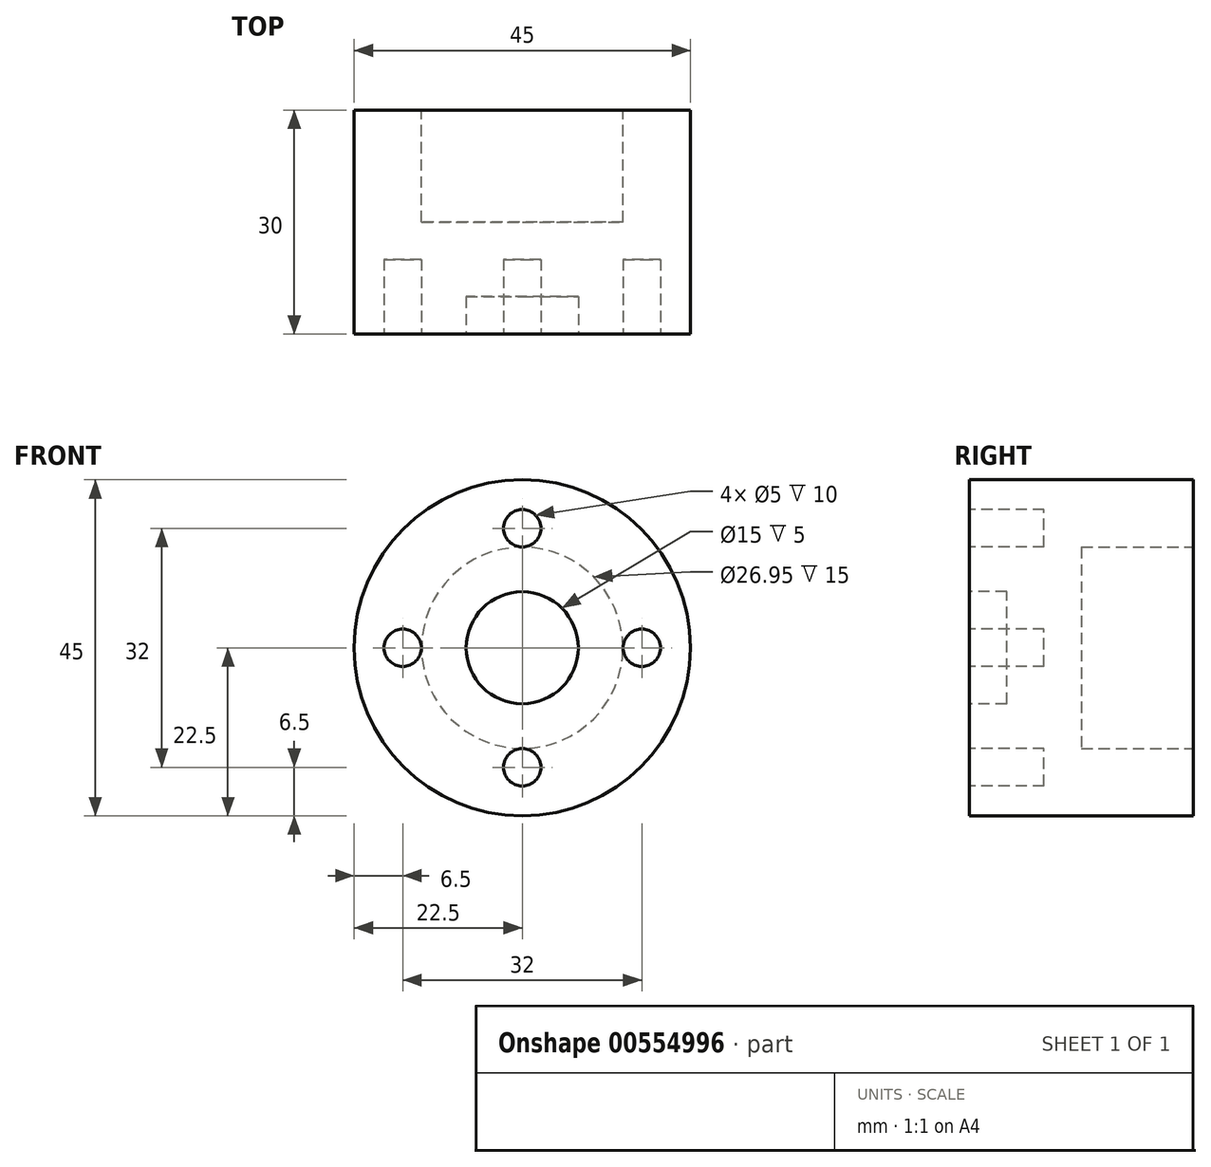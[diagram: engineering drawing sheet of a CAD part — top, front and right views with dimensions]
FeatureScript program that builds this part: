
annotation { "Feature Type Name" : "Feature", "Feature Type Description" : "" }
export const myFeature = defineFeature(function(context is Context, id is Id, definition is map)
    precondition{}
    {
        {
            var Q0;
            Q0=qCreatedBy(makeId("Front.planeOp"),FACE);
            var sketch = newSketch(context, id + "F0", { "sketchPlane" : qUnion([Q0])});
            skCircle(sketch, "E0", {"center": v(0, 0) * mm, "radius": 22.5 * mm});
            skSolve(sketch);
        }
        {
            var Q0;
            Q0=makeQuery(id+"F0.imprint","IMPRINT",FACE,{"disambiguationData":[TD([[makeQuery(id+"F0.imprint","IMPRINT",EDGE,{"derivedFrom":sQuery(id+"F0.wireOp",EDGE,"E0")}),1.0]])]});
            extrude(context, id + "F1", {"entities" : qUnion([Q0]), "depth" : 30 * mm, "offsetDistance" : 25 * mm});
        }
        {
            var Q0;
            Q0=makeQuery(id+"F1.opExtrude","CAP_FACE",FACE,{"disambiguationData":[OSD([sQuery(id+"F0.wireOp",EDGE,"E0")])],"isStart":false});
            var sketch = newSketch(context, id + "F2", { "sketchPlane" : qUnion([Q0])});
            skCircle(sketch, "E1", {"center": v(0, 0) * mm, "radius": 7.5 * mm});
            skSolve(sketch);
        }
        {
            var Q0;
            Q0=makeQuery(id+"F2.imprint","IMPRINT",FACE,{"disambiguationData":[TD([[makeQuery(id+"F2.imprint","IMPRINT",EDGE,{"derivedFrom":sQuery(id+"F2.wireOp",EDGE,"E1")}),1.0]])]});
            extrude(context, id + "F3", {"entities" : qUnion([Q0]), "operationType" : NewBodyOperationType.REMOVE, "oppositeDirection" : true, "depth" : 5 * mm, "offsetDistance" : 25 * mm});
        }
        {
            var Q0;
            Q0=makeQuery(id+"F1.opExtrude","CAP_FACE",FACE,{"disambiguationData":[OSD([sQuery(id+"F0.wireOp",EDGE,"E0")])],"isStart":false});
            var sketch = newSketch(context, id + "F4", { "sketchPlane" : qUnion([Q0])});
            skCircle(sketch, "E2", {"center": v(0, 16) * mm, "radius": 2.5 * mm});
            skCircle(sketch, "E3", {"center": v(0, -16) * mm, "radius": 2.5 * mm});
            skCircle(sketch, "E4", {"center": v(16, 0) * mm, "radius": 2.5 * mm});
            skCircle(sketch, "E5", {"center": v(-16, 0) * mm, "radius": 2.5 * mm});
            skSolve(sketch);
        }
        {
            var Q0;
            Q0=makeQuery(id+"F4.imprint","IMPRINT",FACE,{"disambiguationData":[TD([[makeQuery(id+"F4.imprint","IMPRINT",EDGE,{"derivedFrom":sQuery(id+"F4.wireOp",EDGE,"E5")}),1.0]])]});
            var Q1;
            Q1=makeQuery(id+"F4.imprint","IMPRINT",FACE,{"disambiguationData":[TD([[makeQuery(id+"F4.imprint","IMPRINT",EDGE,{"derivedFrom":sQuery(id+"F4.wireOp",EDGE,"E2")}),1.0]])]});
            var Q2;
            Q2=makeQuery(id+"F4.imprint","IMPRINT",FACE,{"disambiguationData":[TD([[makeQuery(id+"F4.imprint","IMPRINT",EDGE,{"derivedFrom":sQuery(id+"F4.wireOp",EDGE,"E4")}),1.0]])]});
            var Q3;
            Q3=makeQuery(id+"F4.imprint","IMPRINT",FACE,{"disambiguationData":[TD([[makeQuery(id+"F4.imprint","IMPRINT",EDGE,{"derivedFrom":sQuery(id+"F4.wireOp",EDGE,"E3")}),1.0]])]});
            extrude(context, id + "F5", {"entities" : qUnion([Q0, Q1, Q2, Q3]), "operationType" : NewBodyOperationType.REMOVE, "oppositeDirection" : true, "depth" : 10 * mm, "offsetDistance" : 25 * mm});
        }
        {
            var Q0;
            Q0=makeQuery(id+"F1.opExtrude","CAP_FACE",FACE,{"disambiguationData":[OSD([sQuery(id+"F0.wireOp",EDGE,"E0")])],"isStart":true});
            var sketch = newSketch(context, id + "F6", { "sketchPlane" : qUnion([Q0])});
            skCircle(sketch, "E6", {"center": v(0, 0) * mm, "radius": 13.47 * mm});
            skSolve(sketch);
        }
        {
            var Q0;
            Q0=makeQuery(id+"F6.imprint","IMPRINT",FACE,{"disambiguationData":[TD([[makeQuery(id+"F6.imprint","IMPRINT",EDGE,{"derivedFrom":sQuery(id+"F6.wireOp",EDGE,"E6")}),1.0]])]});
            extrude(context, id + "F7", {"entities" : qUnion([Q0]), "operationType" : NewBodyOperationType.REMOVE, "oppositeDirection" : true, "depth" : 15 * mm, "offsetDistance" : 25 * mm});
        }
    });
